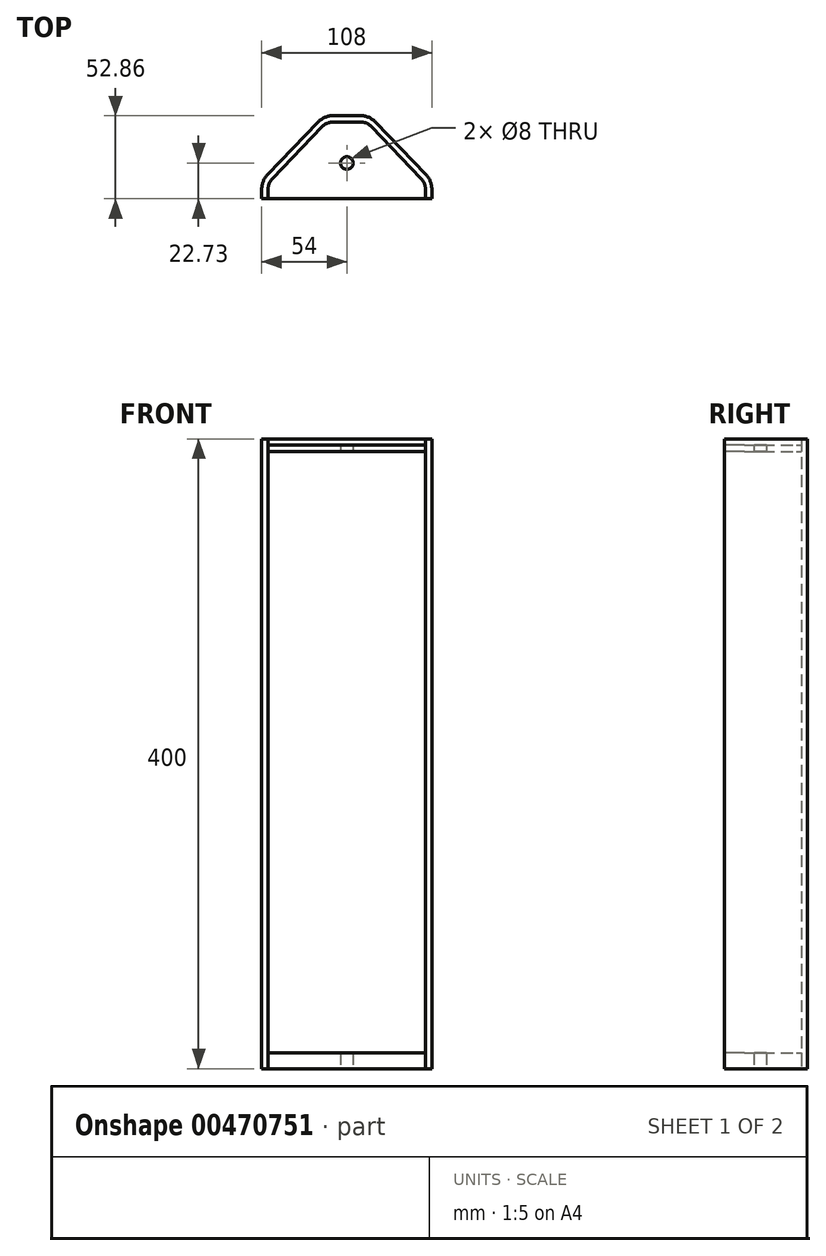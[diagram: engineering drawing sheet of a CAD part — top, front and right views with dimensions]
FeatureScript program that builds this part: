
annotation { "Feature Type Name" : "Feature", "Feature Type Description" : "" }
export const myFeature = defineFeature(function(context is Context, id is Id, definition is map)
    precondition{}
    {
        {
            var Q0;
            Q0=qCreatedBy(makeId("Top.planeOp"),FACE);
            var sketch = newSketch(context, id + "F0", { "sketchPlane" : qUnion([Q0])});
            skCircle(sketch, "E0", {"center": v(0, 0) * mm, "radius": 4 * mm});
            skLineSegment(sketch, "E1", {"start": v(-50, -22.73) * mm, "end": v(50, -22.73) * mm});
            skLineSegment(sketch, "E2", {"start": v(50, -22.73) * mm, "end": v(50, -16.75) * mm});
            skLineSegment(sketch, "E3", {"start": v(47.22, -9.83) * mm, "end": v(15.68, 23.06) * mm});
            skLineSegment(sketch, "E4", {"start": v(-15.68, 23.06) * mm, "end": v(-47.22, -9.83) * mm});
            skLineSegment(sketch, "E5", {"start": v(-50, -16.75) * mm, "end": v(-50, -22.73) * mm});
            skLineSegment(sketch, "E6", {"start": v(-31.9, 6.13) * mm, "end": v(31.9, 6.13) * mm});
            skLineSegment(sketch, "E7", {"start": v(-50, -22.73) * mm, "end": v(0, 6.13) * mm, "construction": true});
            skLineSegment(sketch, "E8", {"start": v(0, 6.13) * mm, "end": v(50, -22.73) * mm, "construction": true});
            skLineSegment(sketch, "E9", {"start": v(-8.46, 26.13) * mm, "end": v(8.46, 26.13) * mm});
            skPoint(sketch, "E10.visualSharp", {"position": v(-50, -12.73) * mm});
            skArc(sketch, "E10.filletArc", {"start": v(-47.22, -9.83) * mm, "mid": v(-49.28, -13.02) * mm, "end": v(-50, -16.75) * mm});
            skPoint(sketch, "E11.visualSharp", {"position": v(-12.73, 26.13) * mm});
            skArc(sketch, "E11.filletArc", {"start": v(-8.46, 26.13) * mm, "mid": v(-12.39, 25.33) * mm, "end": v(-15.68, 23.06) * mm});
            skPoint(sketch, "E12.visualSharp", {"position": v(12.73, 26.13) * mm});
            skArc(sketch, "E12.filletArc", {"start": v(15.68, 23.06) * mm, "mid": v(12.39, 25.33) * mm, "end": v(8.46, 26.13) * mm});
            skPoint(sketch, "E13.visualSharp", {"position": v(50, -12.73) * mm});
            skArc(sketch, "E13.filletArc", {"start": v(50, -16.75) * mm, "mid": v(49.28, -13.02) * mm, "end": v(47.22, -9.83) * mm});
            skLineSegment(sketch, "E14.0", {"start": v(-54, -16.75) * mm, "end": v(-54, -22.73) * mm});
            skArc(sketch, "E14.1", {"start": v(-50.1, -7.06) * mm, "mid": v(-52.99, -11.53) * mm, "end": v(-54, -16.75) * mm});
            skLineSegment(sketch, "E14.2", {"start": v(-18.57, 25.82) * mm, "end": v(-50.1, -7.06) * mm});
            skArc(sketch, "E14.3", {"start": v(-8.46, 30.13) * mm, "mid": v(-13.96, 29.01) * mm, "end": v(-18.57, 25.82) * mm});
            skLineSegment(sketch, "E14.4", {"start": v(-8.46, 30.13) * mm, "end": v(8.46, 30.13) * mm});
            skLineSegment(sketch, "E14.5", {"start": v(54, -22.73) * mm, "end": v(54, -16.75) * mm});
            skArc(sketch, "E14.6", {"start": v(54, -16.75) * mm, "mid": v(52.99, -11.53) * mm, "end": v(50.1, -7.06) * mm});
            skLineSegment(sketch, "E14.7", {"start": v(50.1, -7.06) * mm, "end": v(18.57, 25.82) * mm});
            skArc(sketch, "E14.8", {"start": v(18.57, 25.82) * mm, "mid": v(13.96, 29.01) * mm, "end": v(8.46, 30.13) * mm});
            skLineSegment(sketch, "E15", {"start": v(-54, -22.73) * mm, "end": v(-50, -22.73) * mm});
            skLineSegment(sketch, "E16", {"start": v(50, -22.73) * mm, "end": v(54, -22.73) * mm});
            skSolve(sketch);
        }
        {
            var Q0;
            Q0=makeQuery(id+"F0.imprint","IMPRINT",FACE,{"disambiguationData":[TD([[makeQuery(id+"F0.imprint","IMPRINT",EDGE,{"derivedFrom":sQuery(id+"F0.wireOp",EDGE,"E2")}),-1.0]])]});
            extrude(context, id + "F1", {"entities" : qUnion([Q0]), "depth" : 400 * mm});
        }
        {
            var Q0;
            Q0=makeQuery(id+"F0.imprint","IMPRINT",FACE,{"disambiguationData":[TD([[makeQuery(id+"F0.imprint","IMPRINT",EDGE,{"derivedFrom":sQuery(id+"F0.wireOp",EDGE,"E0")}),-1.0]])]});
            var Q1;
            {var subQ0=sQuery(id+"F0.wireOp",EDGE,"E6");Q1=makeQuery(id+"F0.imprint","IMPRINT",FACE,{"disambiguationData":[TD([[makeQuery(id+"F0.imprint","IMPRINT",EDGE,{"derivedFrom":subQ0}),1.0]])]});}
            extrude(context, id + "F2", {"entities" : qUnion([Q0, Q1]), "depth" : 10 * mm});
        }
        {
            var Q0;
            Q0=makeQuery(id+"F2.opExtrude","CAP_FACE",FACE,{"disambiguationData":[OSD([sQuery(id+"F0.wireOp",EDGE,"E0"),sQuery(id+"F0.wireOp",EDGE,"E1"),sQuery(id+"F0.wireOp",EDGE,"E2"),sQuery(id+"F0.wireOp",EDGE,"E3"),sQuery(id+"F0.wireOp",EDGE,"E4"),sQuery(id+"F0.wireOp",EDGE,"E5"),sQuery(id+"F0.wireOp",EDGE,"E9"),sQuery(id+"F0.wireOp",EDGE,"E10.filletArc"),sQuery(id+"F0.wireOp",EDGE,"E11.filletArc"),sQuery(id+"F0.wireOp",EDGE,"E12.filletArc"),sQuery(id+"F0.wireOp",EDGE,"E13.filletArc")])],"isStart":false});
            extrude(context, id + "F3", {"entities" : qUnion([Q0]), "depth" : 386 * mm, "hasSecondDirection" : true, "secondDirectionOppositeDirection" : false, "secondDirectionDepth" : 382 * mm});
        }
    });
